# Revit family: Cabinet_Wenger_UltraStor_42
name_source: partatom
category: Furniture
revit_build: Autodesk Revit 2015 (Build: 20140606_1530(x64)
units: mm (PartAtom-declared; Revit-internal decimal feet)

## types (6) — shared parameters
Assembly Code = E2010200
Cabinet Back Thickness = 0' - 3 1/4"
Cabinet Height = 7' - 1 5/8"
Cabinet Width = 5' - 0 1/2"
Construction Details = http://www.arcat.com
Door Height = 6' - 8 7/8"
Door Width = 2' - 5 7/16"
Green Building-LEED = http://www.arcat.com
Keynote = 12 35 83
Manufacturer = Wenger Corporation
Manufacturer Fax = (507) 455-4258
Manufacturer Website = https://www.wengercorp.com
Product Data = http://www.arcat.com
Revision = R1_2018-04
Sales Information = https://www.wengercorp.com
Specification = http://www.arcat.com
URL = https://www.wengercorp.com
zero-valued in all types: Cost

## per-type parameters (varying)
| type | Description | Door Style | HasDoors | Installed Depth | Model | Rear Panel Thickness |
| Acoustic Cabinet #42 - Grille Door | Wenger Acoustic Cabinet #42 - Comp Grille Doors | Door_FullHt : Bars | Yes | 3' - 6" | #42A | 0' - 3 1/4" |
| Acoustic Cabinet #42 - Waterfall Door | Wenger Acoustic Cabinet #42 - Comp Waterfall Grille Doors | Door_FullHt : Waterfall | Yes | 3' - 6" | #42A | 0' - 3 1/4" |
| Acoustic Cabinet #42 - No Door | Wenger Acoustic Cabinet #42 - No Doors | Door_FullHt : Solid Door | No | 3' - 6" | #42A | 0' - 3 1/4" |
| UltraStor Cabinet #42 - Grille Door | Wenger UltraStor Cabinet #42 - Comp Grille Doors | Door_FullHt : Bars | Yes | 3' - 3 1/2" | #42 | 0' - 0 3/4" |
| UltraStor Cabinet #42 - Waterfall Door | Wenger UltraStor Cabinet #42 - Comp Waterfall Grille Doors | Door_FullHt : Waterfall | Yes | 3' - 3 1/2" | #42 | 0' - 0 3/4" |
| UltraStor Cabinet #42 - No Door | Wenger UltraStor Cabinet #42 - No Doors | Door_FullHt : Solid Door | No | 3' - 3 1/2" | #42 | 0' - 0 3/4" |

## geometry (parser evidence)
native form markers: Blend x16, Sweep x35
no freeform markers — native parametric forms only
